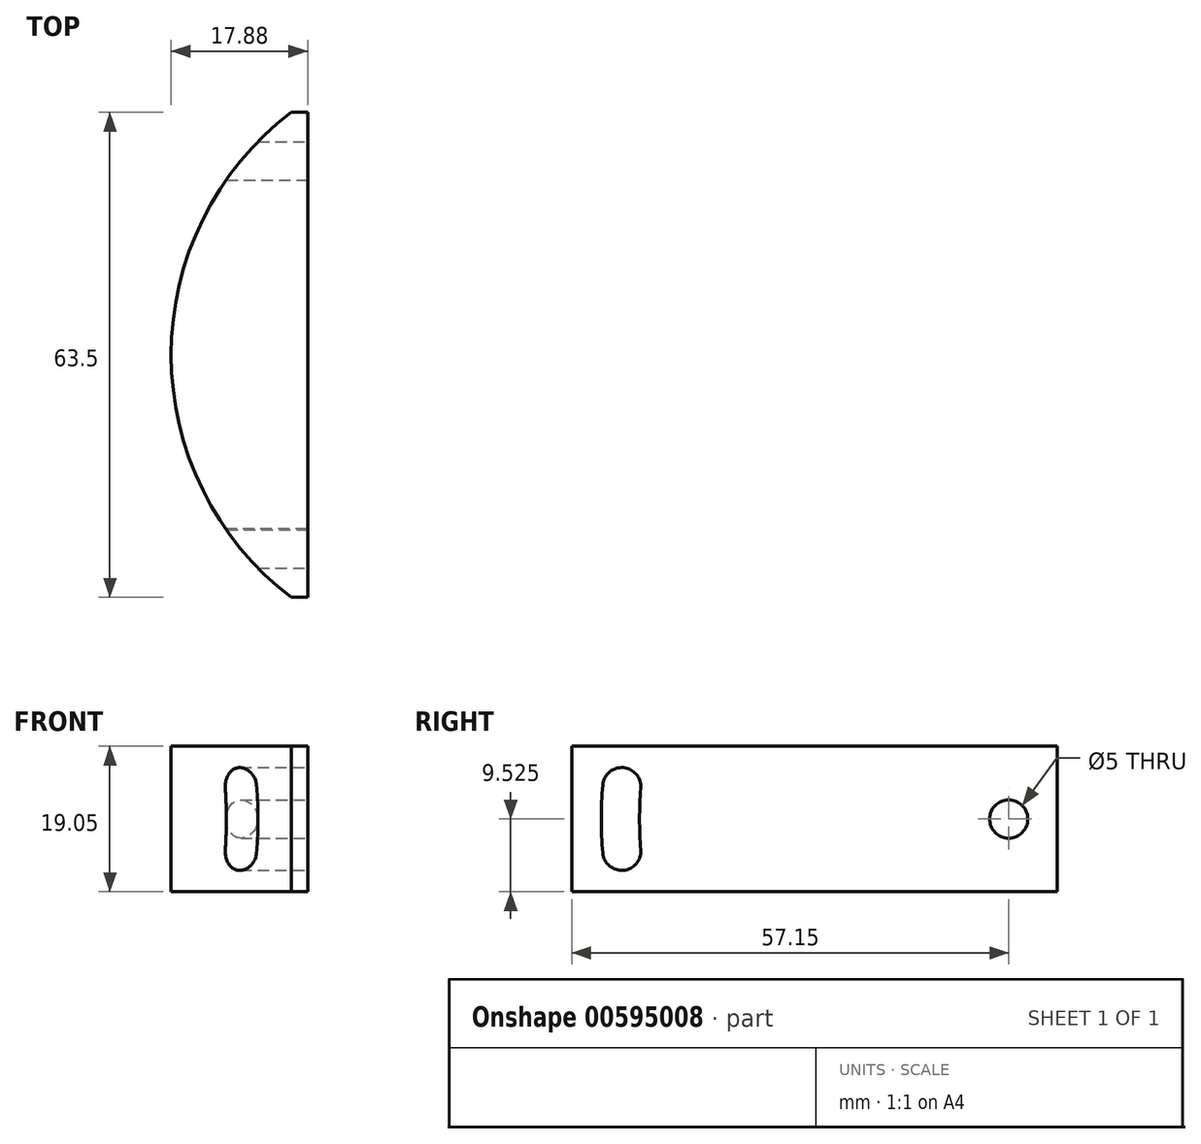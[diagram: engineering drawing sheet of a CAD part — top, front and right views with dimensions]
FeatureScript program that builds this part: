
annotation { "Feature Type Name" : "Feature", "Feature Type Description" : "" }
export const myFeature = defineFeature(function(context is Context, id is Id, definition is map)
    precondition{}
    {
        {
            var Q0;
            Q0=qCreatedBy(makeId("Top.planeOp"),FACE);
            var sketch = newSketch(context, id + "F0", { "sketchPlane" : qUnion([Q0])});
            skArc(sketch, "E0", {"start": v(-24.24, 31.75) * mm, "mid": v(-39.95, 0) * mm, "end": v(-24.24, -31.75) * mm});
            skLineSegment(sketch, "E1", {"start": v(-22.07, 31.75) * mm, "end": v(-22.07, -31.75) * mm});
            skLineSegment(sketch, "E2", {"start": v(-22.07, -31.75) * mm, "end": v(-24.24, -31.75) * mm});
            skLineSegment(sketch, "E3", {"start": v(-22.07, 31.75) * mm, "end": v(-24.24, 31.75) * mm});
            skPoint(sketch, "E4", {"position": v(-22.07, 0) * mm});
            skSolve(sketch);
        }
        {
            var Q0;
            Q0=makeQuery(id+"F0.imprint","IMPRINT",FACE,{"disambiguationData":[TD([[makeQuery(id+"F0.imprint","IMPRINT",EDGE,{"derivedFrom":sQuery(id+"F0.wireOp",EDGE,"E0")}),1.0]])]});
            extrude(context, id + "F1", {"entities" : qUnion([Q0]), "depth" : 19.05 * mm, "offsetDistance" : 25.4 * mm});
        }
        {
            var Q0;
            Q0=makeQuery(id+"F1.opExtrude","SWEPT_FACE",FACE,{"disambiguationData":[OSD([sQuery(id+"F0.wireOp",EDGE,"E1")])]});
            var sketch = newSketch(context, id + "F2", { "sketchPlane" : qUnion([Q0])});
            skLineSegment(sketch, "E5", {"start": v(-31.75, 17.15) * mm, "end": v(-31.75, 1.9) * mm});
            skPoint(sketch, "E6", {"position": v(-31.75, 9.53) * mm});
            skLineSegment(sketch, "E7", {"start": v(-31.75, 9.53) * mm, "end": v(26.83, 9.53) * mm});
            skPoint(sketch, "E8", {"position": v(-25.4, 9.53) * mm});
            skPoint(sketch, "E9", {"position": v(25.4, 9.53) * mm});
            skArc(sketch, "E10", {"start": v(-22.73, 13.55) * mm, "mid": v(-25.02, 16.25) * mm, "end": v(-27.72, 13.97) * mm});
            skArc(sketch, "E11.MirrorCS", {"start": v(-22.73, 5.5) * mm, "mid": v(-25.02, 2.8) * mm, "end": v(-27.72, 5.08) * mm});
            skPoint(sketch, "E12.MirrorCS.end.orphan", {"position": v(-27.88, 9.53) * mm});
            skPoint(sketch, "E12.MirrorCS.start.orphan", {"position": v(-44.28, 25.45) * mm});
            skPoint(sketch, "E13.MirrorCS.end.orphan", {"position": v(-22.88, 9.53) * mm});
            skPoint(sketch, "E13.MirrorCS.start.orphan", {"position": v(-22.73, 5.5) * mm});
            skArc(sketch, "E14", {"start": v(-22.73, 13.55) * mm, "mid": v(-22.9, 9.53) * mm, "end": v(-22.73, 5.5) * mm});
            skArc(sketch, "E15", {"start": v(-27.72, 13.97) * mm, "mid": v(-27.9, 9.53) * mm, "end": v(-27.72, 5.08) * mm});
            skSolve(sketch);
        }
        {
            var Q0;
            Q0=qSketchRegion(id+"F2",true);
            extrude(context, id + "F3", {"entities" : qUnion([Q0]), "operationType" : NewBodyOperationType.REMOVE, "oppositeDirection" : true, "depth" : 25.4 * mm, "offsetDistance" : 25.4 * mm});
        }
        {
            var Q0;
            Q0=sQuery(id+"F2.wireOp",VERTEX,"E9");
            var Q1;
            Q1=makeQuery(id+"F1.opExtrude","SWEPT_BODY",BODY,{"disambiguationData":[OSD([sQuery(id+"F0.wireOp",EDGE,"E0"),sQuery(id+"F0.wireOp",EDGE,"E1"),sQuery(id+"F0.wireOp",EDGE,"E2"),sQuery(id+"F0.wireOp",EDGE,"E3")])]});
            hole(context, id + "F4", {"style" : HoleStyle.SIMPLE, "endStyle" : HoleEndStyle.BLIND, "standardTappedOrClearance" : lookupTablePath({ "standard" : "ISO", "engagement" : "75%", "pitch" : "1 mm", "size" : "M6", "type" : "Tapped" }), "standardBlindInLast" : lookupTablePath({ "standard" : "ISO", "engagement" : "75%", "pitch" : "1 mm", "size" : "M6", "type" : "Tapped" }), "holeDiameter" : 5 * mm, "showTappedDepth" : true, "holeDepth" : 15.7 * mm, "isTappedThrough" : true, "tappedDepth" : 12.7 * mm, "tapClearance" : 3, "locations" : qUnion([Q0]), "scope" : qUnion([Q1]), "majorDiameter" : 6 * mm});
        }
    });
